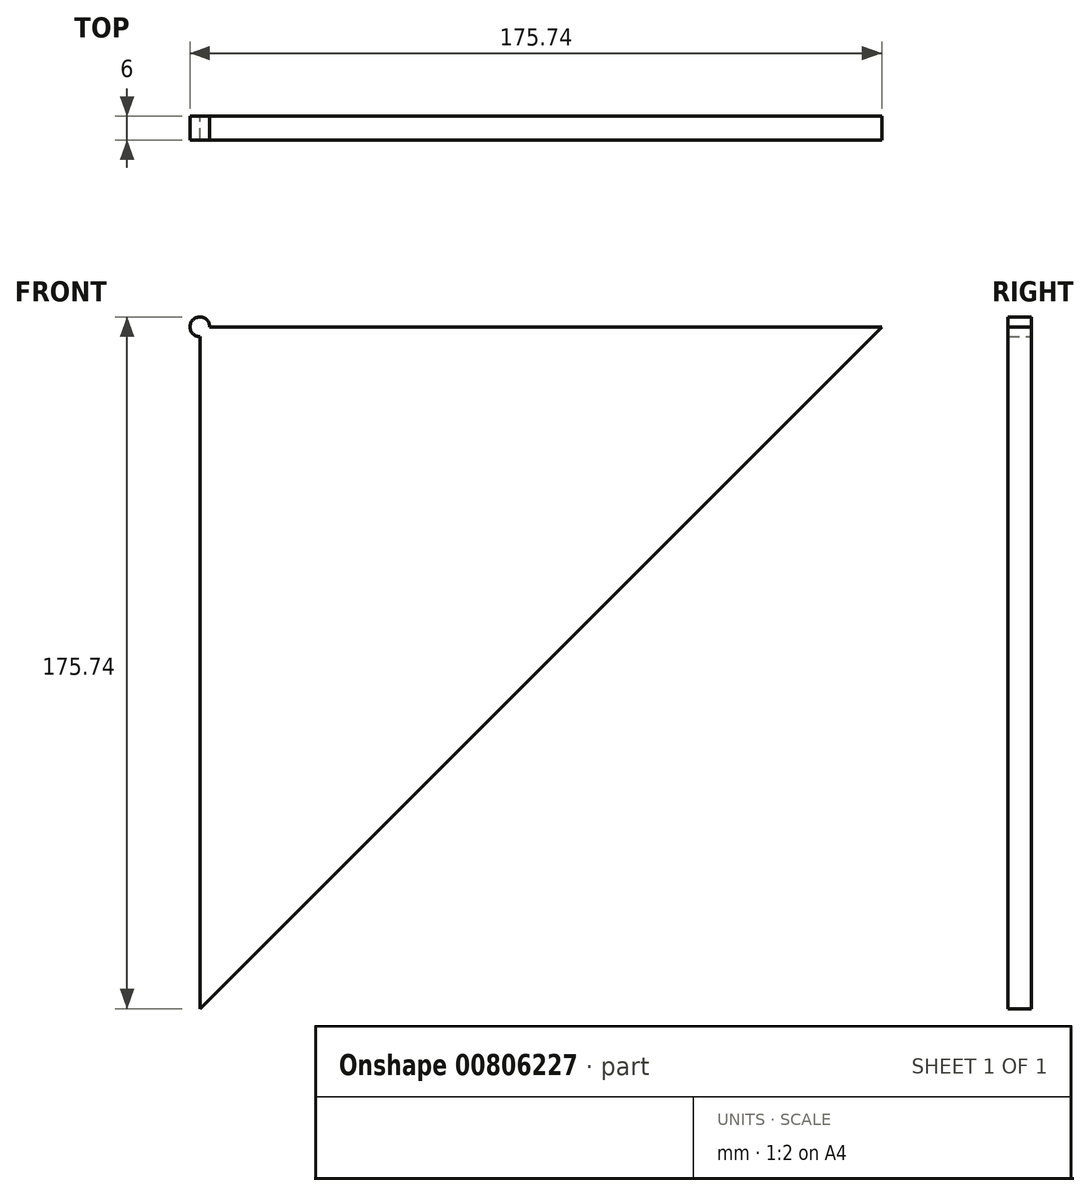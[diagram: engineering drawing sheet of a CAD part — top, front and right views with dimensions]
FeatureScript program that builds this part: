
annotation { "Feature Type Name" : "Feature", "Feature Type Description" : "" }
export const myFeature = defineFeature(function(context is Context, id is Id, definition is map)
    precondition{}
    {
        {
            var Q0;
            Q0=qCreatedBy(makeId("Front.planeOp"),FACE);
            var sketch = newSketch(context, id + "F0", { "sketchPlane" : qUnion([Q0])});
            skLineSegment(sketch, "E0", {"start": v(0, 0) * mm, "end": v(1.77, -1.77) * mm});
            skLineSegment(sketch, "E1", {"start": v(228.04, -228.04) * mm, "end": v(121.98, -121.98) * mm});
            skLineSegment(sketch, "E2", {"start": v(0, 0) * mm, "end": v(2.5, 0) * mm});
            skLineSegment(sketch, "E3", {"start": v(0, 0) * mm, "end": v(0, -2.5) * mm});
            skLineSegment(sketch, "E4", {"start": v(121.98, -121.98) * mm, "end": v(243.95, 0) * mm});
            skLineSegment(sketch, "E5", {"start": v(121.98, -121.98) * mm, "end": v(0, -243.95) * mm});
            skLineSegment(sketch, "E6", {"start": v(228.04, -228.04) * mm, "end": v(456.08, 0) * mm});
            skLineSegment(sketch, "E7", {"start": v(228.04, -228.04) * mm, "end": v(0, -456.08) * mm});
            skCircle(sketch, "E8", {"center": v(0, 0) * mm, "radius": 2.5 * mm});
            skLineSegment(sketch, "E9.trimOffspring", {"start": v(243.95, 0) * mm, "end": v(456.08, 0) * mm});
            skLineSegment(sketch, "E10.trimOffspring", {"start": v(0, -243.95) * mm, "end": v(0, -456.08) * mm});
            skLineSegment(sketch, "E11.trimOffspring", {"start": v(121.98, -121.98) * mm, "end": v(228.04, -228.04) * mm});
            skLineSegment(sketch, "E12", {"start": v(0, -243.95) * mm, "end": v(0, 0) * mm});
            skLineSegment(sketch, "E13", {"start": v(173.24, 0) * mm, "end": v(0, 0) * mm});
            skLineSegment(sketch, "E14.0", {"start": v(0, -173.24) * mm, "end": v(173.24, 0) * mm});
            skLineSegment(sketch, "E14.1", {"start": v(-1212.55, -1385.8) * mm, "end": v(-1318.62, -1491.86) * mm});
            skSolve(sketch);
        }
        {
            var Q0;
            {var subQ1=sQuery(id+"F0.wireOp",EDGE,"E2");var subQ3=sQuery(id+"F0.wireOp",EDGE,"E8");var subQ4=makeQuery(id+"F0.imprint","INTERSECT",VERTEX,{"derivedFrom":[subQ1,subQ3]});Q0=makeQuery(id+"F0.imprint","IMPRINT",FACE,{"disambiguationData":[TD([[makeQuery(id+"F0.imprint","IMPRINT",EDGE,{"disambiguationData":[TD([[subQ4,-1.0]])],"derivedFrom":subQ3}),1.0]])]});}
            var Q1;
            {var subQ0=sQuery(id+"F0.wireOp",EDGE,"E3");var subQ3=sQuery(id+"F0.wireOp",EDGE,"E8");var subQ5=makeQuery(id+"F0.imprint","INTERSECT",VERTEX,{"derivedFrom":[subQ0,subQ3]});Q1=makeQuery(id+"F0.imprint","IMPRINT",FACE,{"disambiguationData":[TD([[makeQuery(id+"F0.imprint","IMPRINT",EDGE,{"disambiguationData":[TD([[subQ5,-1.0]])],"derivedFrom":subQ3}),1.0]])]});}
            var Q2;
            {var subQ0=sQuery(id+"F0.wireOp",EDGE,"E2");var subQ3=sQuery(id+"F0.wireOp",EDGE,"E8");var subQ5=makeQuery(id+"F0.imprint","INTERSECT",VERTEX,{"derivedFrom":[subQ0,subQ3]});Q2=makeQuery(id+"F0.imprint","IMPRINT",FACE,{"disambiguationData":[TD([[makeQuery(id+"F0.imprint","IMPRINT",EDGE,{"disambiguationData":[TD([[subQ5,1.0]])],"derivedFrom":subQ3}),1.0]])]});}
            extrude(context, id + "F1", {"entities" : qUnion([Q0, Q1, Q2]), "depth" : 6 * mm, "offsetDistance" : 25 * mm});
        }
        {
            var Q0;
            {var subQ0=sQuery(id+"F0.wireOp",EDGE,"E14.0");Q0=makeQuery(id+"F0.imprint","IMPRINT",FACE,{"disambiguationData":[TD([[makeQuery(id+"F0.imprint","IMPRINT",EDGE,{"derivedFrom":subQ0}),1.0]])]});}
            extrude(context, id + "F2", {"entities" : qUnion([Q0]), "operationType" : NewBodyOperationType.ADD, "depth" : 6 * mm, "offsetDistance" : 25 * mm});
        }
    });
